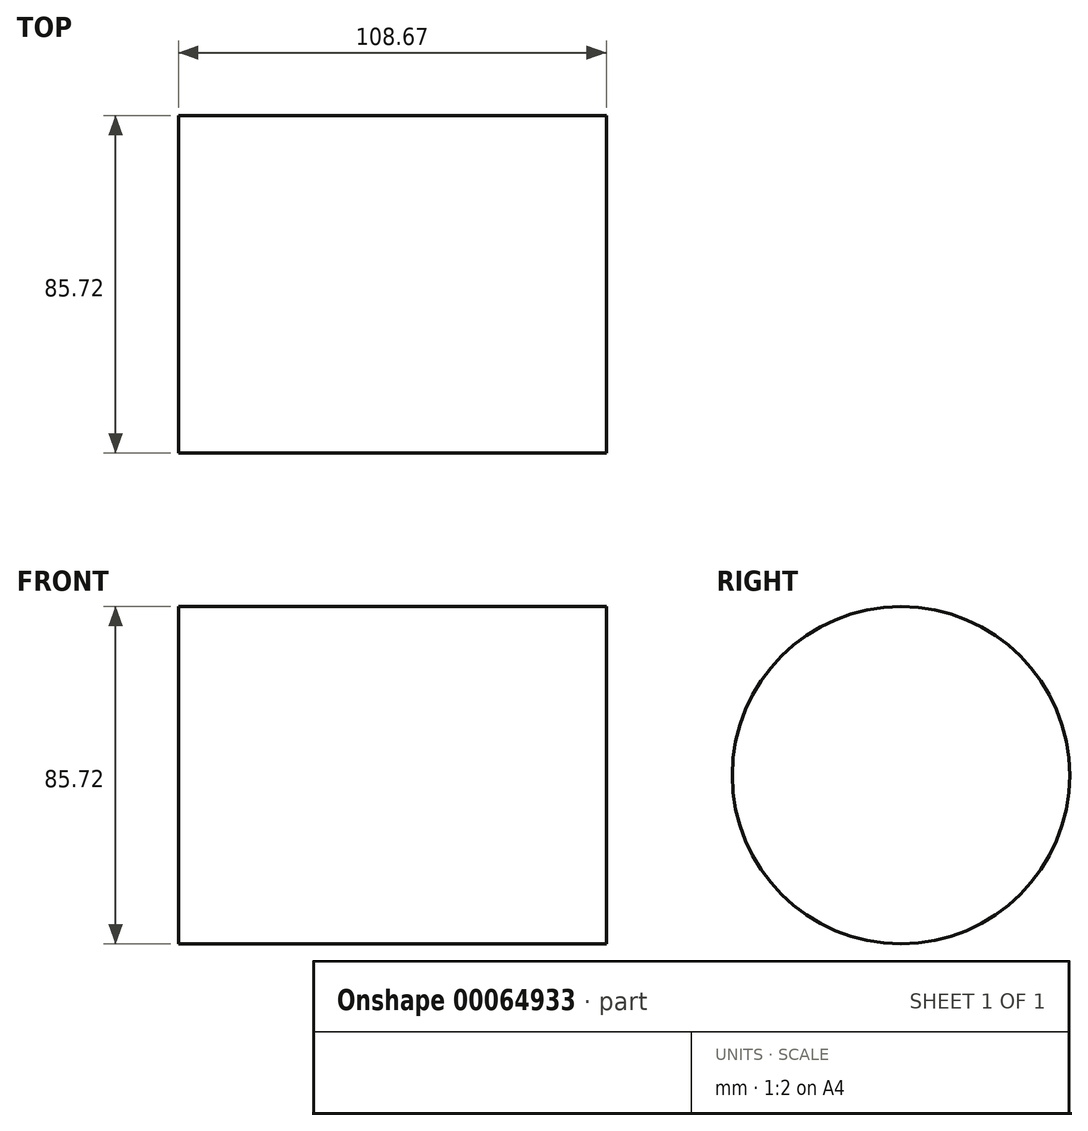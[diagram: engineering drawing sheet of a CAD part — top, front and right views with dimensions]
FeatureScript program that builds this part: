
annotation { "Feature Type Name" : "Feature", "Feature Type Description" : "" }
export const myFeature = defineFeature(function(context is Context, id is Id, definition is map)
    precondition{}
    {
        {
            var Q0;
            Q0=qCreatedBy(makeId("Front.planeOp"),FACE);
            var sketch = newSketch(context, id + "F0", { "sketchPlane" : qUnion([Q0])});
            skLineSegment(sketch, "E0.bottom", {"start": v(0, 0) * mm, "end": v(-108.67, 0) * mm});
            skLineSegment(sketch, "E0.top", {"start": v(0, 42.86) * mm, "end": v(-108.67, 42.86) * mm});
            skLineSegment(sketch, "E0.left", {"start": v(0, 0) * mm, "end": v(0, 42.86) * mm});
            skLineSegment(sketch, "E0.right", {"start": v(-108.67, 0) * mm, "end": v(-108.67, 42.86) * mm});
            skSolve(sketch);
        }
        {
            var Q0;
            Q0=makeQuery(id+"F0.imprint","IMPRINT",FACE,{"disambiguationData":[TD([[makeQuery(id+"F0.imprint","IMPRINT",EDGE,{"derivedFrom":sQuery(id+"F0.wireOp",EDGE,"E0.bottom")}),-1.0]])]});
            var Q1;
            Q1=sQuery(id+"F0.wireOp",EDGE,"E0.bottom");
            revolve(context, id + "F1", {"entities" : qUnion([Q0]), "axis" : qUnion([Q1]), "revolveType" : RevolveType.FULL});
        }
    });
